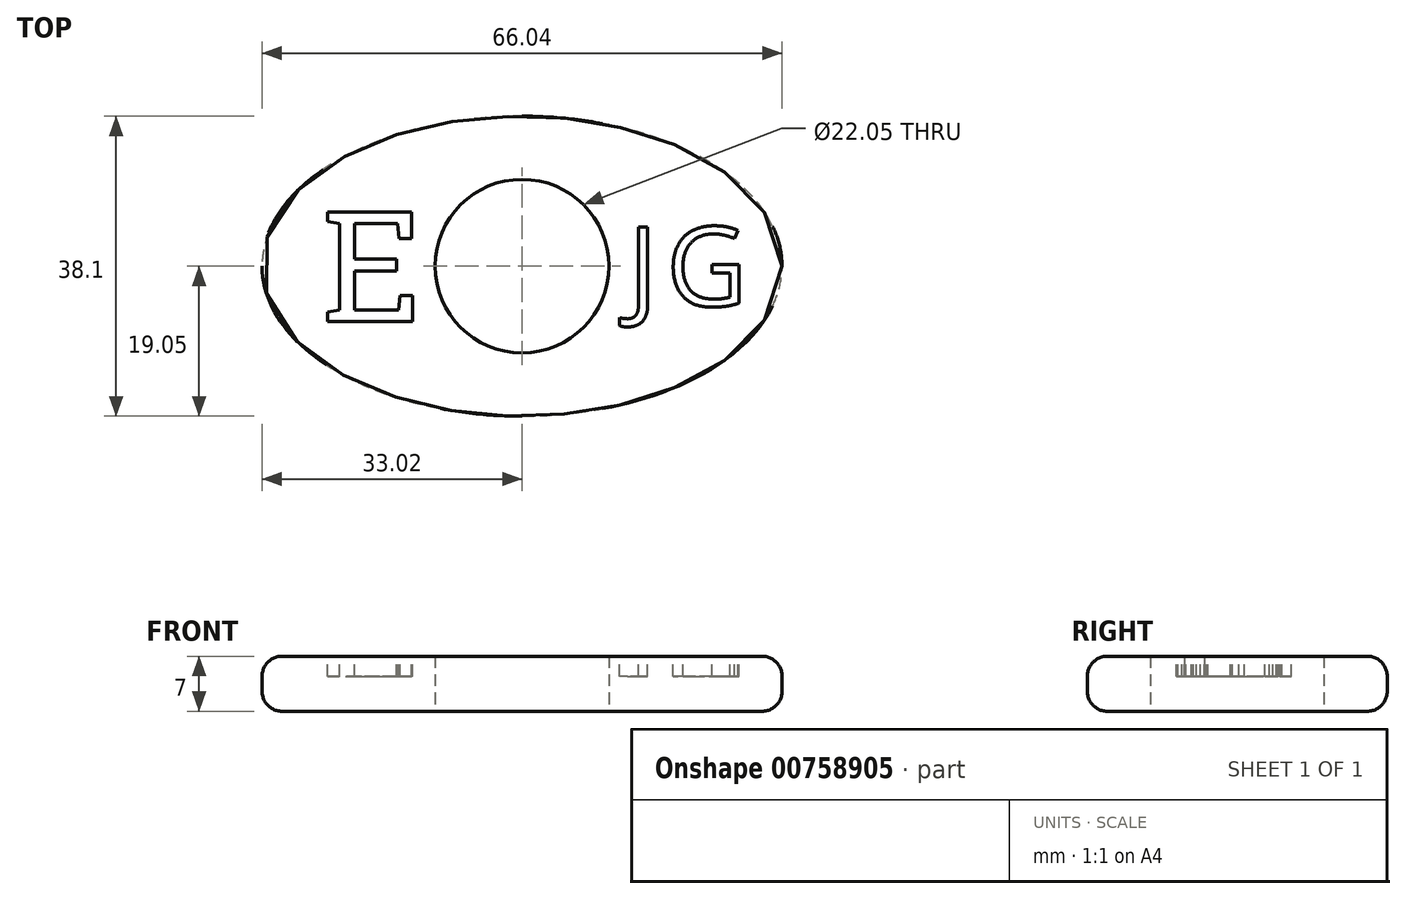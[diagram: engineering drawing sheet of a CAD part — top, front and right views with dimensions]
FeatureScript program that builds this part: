
annotation { "Feature Type Name" : "Feature", "Feature Type Description" : "" }
export const myFeature = defineFeature(function(context is Context, id is Id, definition is map)
    precondition{}
    {
        {
            var Q0;
            Q0=qCreatedBy(makeId("Top.planeOp"),FACE);
            var sketch = newSketch(context, id + "F0", { "sketchPlane" : qUnion([Q0])});
            skEllipse(sketch, "E0", {"center": v(0, 0) * mm, "majorRadius": 33.02 * mm, "minorRadius": 19.05 * mm, "majorAxis": v(1, 0)});
            skCircle(sketch, "E1", {"center": v(0, 0) * mm, "radius": 11.03 * mm});
            skLineSegment(sketch, "E2", {"start": v(-33.02, 0) * mm, "end": v(33.02, 0) * mm, "construction": true});
            skLineSegment(sketch, "E3", {"start": v(0, 19.05) * mm, "end": v(0, -19.05) * mm, "construction": true});
            skSolve(sketch);
        }
        {
            var Q0;
            Q0=makeQuery(id+"F0.imprint","IMPRINT",FACE,{"disambiguationData":[TD([[makeQuery(id+"F0.imprint","IMPRINT",EDGE,{"derivedFrom":sQuery(id+"F0.wireOp",EDGE,"E0")}),1.0]])]});
            extrude(context, id + "F1", {"entities" : qUnion([Q0]), "depth" : 7 * mm, "offsetDistance" : 25.4 * mm});
        }
        {
            var Q0;
            Q0=makeQuery(id+"F1.opExtrude","CAP_EDGE",EDGE,{"disambiguationData":[OSD([sQuery(id+"F0.wireOp",EDGE,"E0")])],"isStart":false});
            var Q1;
            Q1=makeQuery(id+"F1.opExtrude","CAP_EDGE",EDGE,{"disambiguationData":[OSD([sQuery(id+"F0.wireOp",EDGE,"E0")])],"isStart":true});
            fillet(context, id + "F2", {"entities" : qUnion([Q0, Q1]), "radius" : 2.54 * mm, "tangentPropagation" : true, "allowEdgeOverflow" : false});
        }
        {
            var Q0;
            Q0=makeQuery(id+"F1.opExtrude","CAP_FACE",FACE,{"disambiguationData":[OSD([sQuery(id+"F0.wireOp",EDGE,"E0"),sQuery(id+"F0.wireOp",EDGE,"E1")])],"isStart":false});
            var sketch = newSketch(context, id + "F3", { "sketchPlane" : qUnion([Q0])});
            skSolve(sketch);
        }
        {
            var Q0;
            {var subQ0=sQuery(id+"F0.wireOp",EDGE,"E1");Q0=makeQuery(id+"F3.imprint","IMPRINT",FACE,{"disambiguationData":[TD([[makeQuery(id+"F3.imprint","IMPRINT",EDGE,{"derivedFrom":makeQuery(id+"F1.opExtrude","CAP_EDGE",EDGE,{"disambiguationData":[OSD([subQ0])],"isStart":false})}),-1.0]])]});}
            var sketch = newSketch(context, id + "F4", { "sketchPlane" : qUnion([Q0])});
            skText(sketch, "E4", { "text": "E", "fontName": "RobotoSlab-Regular.ttf"});
            skLineSegment(sketch, "E5", {"start": v(0, 0) * mm, "end": v(-25.4, 0) * mm, "construction": true});
            skLineSegment(sketch, "E6", {"start": v(-25.4, 0) * mm, "end": v(-12.7, 0) * mm, "construction": true});
            skPoint(sketch, "E7", {"position": v(19.05, 0) * mm});
            skPoint(sketch, "E8", {"position": v(-19.05, 0) * mm});
            skText(sketch, "E9", { "text": "J", "fontName": "OpenSans-Regular.ttf"});
            skText(sketch, "E10", { "text": "G", "fontName": "OpenSans-Regular.ttf"});
            skLineSegment(sketch, "E11", {"start": v(13.47, 0) * mm, "end": v(17.96, 0) * mm, "construction": true});
            skPoint(sketch, "E12", {"position": v(15.71, 0) * mm});
            skPoint(sketch, "E13", {"position": v(23.42, 0) * mm});
            const initialGuessF4  = {"E4": [-0.0254, -0.00706, 1, 0, 0.01411], "E9": [0.01347, -0.00508, 1, 0, 0.01016], "E10": [0.01834, -0.00508, 1, 0, 0.01016]};
            skSetInitialGuess(sketch, initialGuessF4);
            skSolve(sketch);
        }
        {
            var Q0;
            Q0 = qSketchRegion(id + "F4", true);
            extrude(context, id + "F5", {"entities" : qUnion([Q0]), "operationType" : NewBodyOperationType.REMOVE, "oppositeDirection" : true, "depth" : 2.54 * mm, "offsetDistance" : 25.4 * mm});
        }
    });
